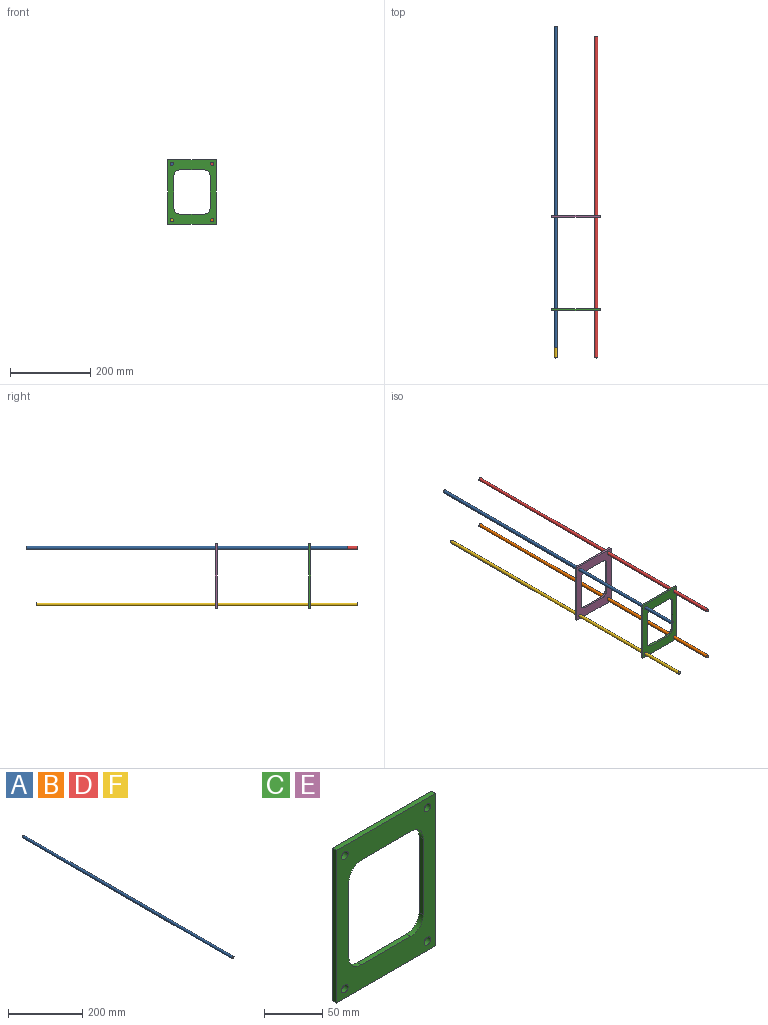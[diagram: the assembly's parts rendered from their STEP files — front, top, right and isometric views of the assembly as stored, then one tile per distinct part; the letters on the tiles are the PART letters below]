
ASSEMBLY  parts=6 mates=7
PART A: 3 faces, bbox 8x800x8 mm
  f0: cylinder r=4mm len=800mm, axis (0,1,0), area 20106.2mm2, adj f1,f2
  f1: plane 8x8mm, normal (0,-1,0), area 50.3mm2, adj f0
  f2: plane 8x8mm, normal (0,1,0), area 50.3mm2, adj f0
PART B: same geometry as A
PART C: 18 faces, bbox 120x5x160 mm
  f0: plane 120x5mm, normal (0,0,1), area 600mm2, adj f1,f15,f16,f17
  f1: plane 160x5mm, normal (-1,0,0), area 800mm2, adj f0,f2,f16,f17
  f2: plane 120x5mm, normal (0,0,-1), area 600mm2, adj f1,f15,f16,f17
  f3: cylinder r=15mm len=15mm, axis (0,1,0), area 117.8mm2, adj f4,f10,f16,f17
  f4: plane 60x5mm, normal (0,0,-1), area 300mm2, adj f3,f5,f16,f17
  f5: cylinder r=15mm len=15mm, axis (0,1,0), area 117.8mm2, adj f4,f6,f16,f17
  f6: plane 80x5mm, normal (-1,0,0), area 400mm2, adj f5,f7,f16,f17
  f7: cylinder r=15mm len=15mm, axis (0,1,0), area 117.8mm2, adj f6,f8,f16,f17
  f8: plane 60x5mm, normal (0,0,1), area 300mm2, adj f7,f9,f16,f17
  f9: cylinder r=15mm len=15mm, axis (0,1,0), area 117.8mm2, adj f8,f10,f16,f17
  f10: plane 80x5mm, normal (1,0,0), area 400mm2, adj f3,f9,f16,f17
  f11: cylinder r=4mm len=8mm, axis (0,1,0), area 125.7mm2, adj f16,f17
  f12: cylinder r=4mm len=8mm, axis (0,1,0), area 125.7mm2, adj f16,f17
  f13: cylinder r=4mm len=8mm, axis (0,1,0), area 125.7mm2, adj f16,f17
  f14: cylinder r=4mm len=8mm, axis (0,1,0), area 125.7mm2, adj f16,f17
  f15: plane 160x5mm, normal (1,0,0), area 800mm2, adj f0,f2,f16,f17
  f16: plane 160x120mm, normal (0,-1,0), area 9292.1mm2, adj f0,f1,f2,f3,f4,f5,f6,f7
  f17: plane 160x120mm, normal (0,1,0), area 9292.1mm2, adj f0,f1,f2,f3,f4,f5,f6,f7
PART D: same geometry as A
PART E: same geometry as C
PART F: same geometry as A
PLACE A t=(-290.02,635.32,3.65)mm
PLACE B t=(-190.02,610.28,-136.35)mm
PLACE C t=(-240.02,-67.26,-66.35)mm fixed
PLACE D t=(-190.02,610.28,3.65)mm
PLACE E t=(-240.02,164.58,-66.35)mm
PLACE F t=(-290.02,610.28,-136.35)mm
MATE slider D.f0 <-> E.f14  axis (0,1,0) through (-190.02,610.28,3.65)mm
MATE slider B.f0 <-> E.f13  axis (0,1,0) through (-190.02,610.28,-136.35)mm
MATE slider D.f0 <-> C.f14  axis (0,-1,0) through (-190.02,-189.72,3.65)mm
MATE slider F.f0 <-> E.f12  axis (0,1,0) through (-290.02,610.28,-136.35)mm
MATE slider A.f0 <-> C.f11  axis (0,-1,0) through (-290.02,-164.68,3.65)mm
MATE slider F.f0 <-> C.f12  axis (0,-1,0) through (-290.02,-189.72,-136.35)mm
MATE slider B.f0 <-> C.f13  axis (0,1,0) through (-190.02,-189.72,-136.35)mm
